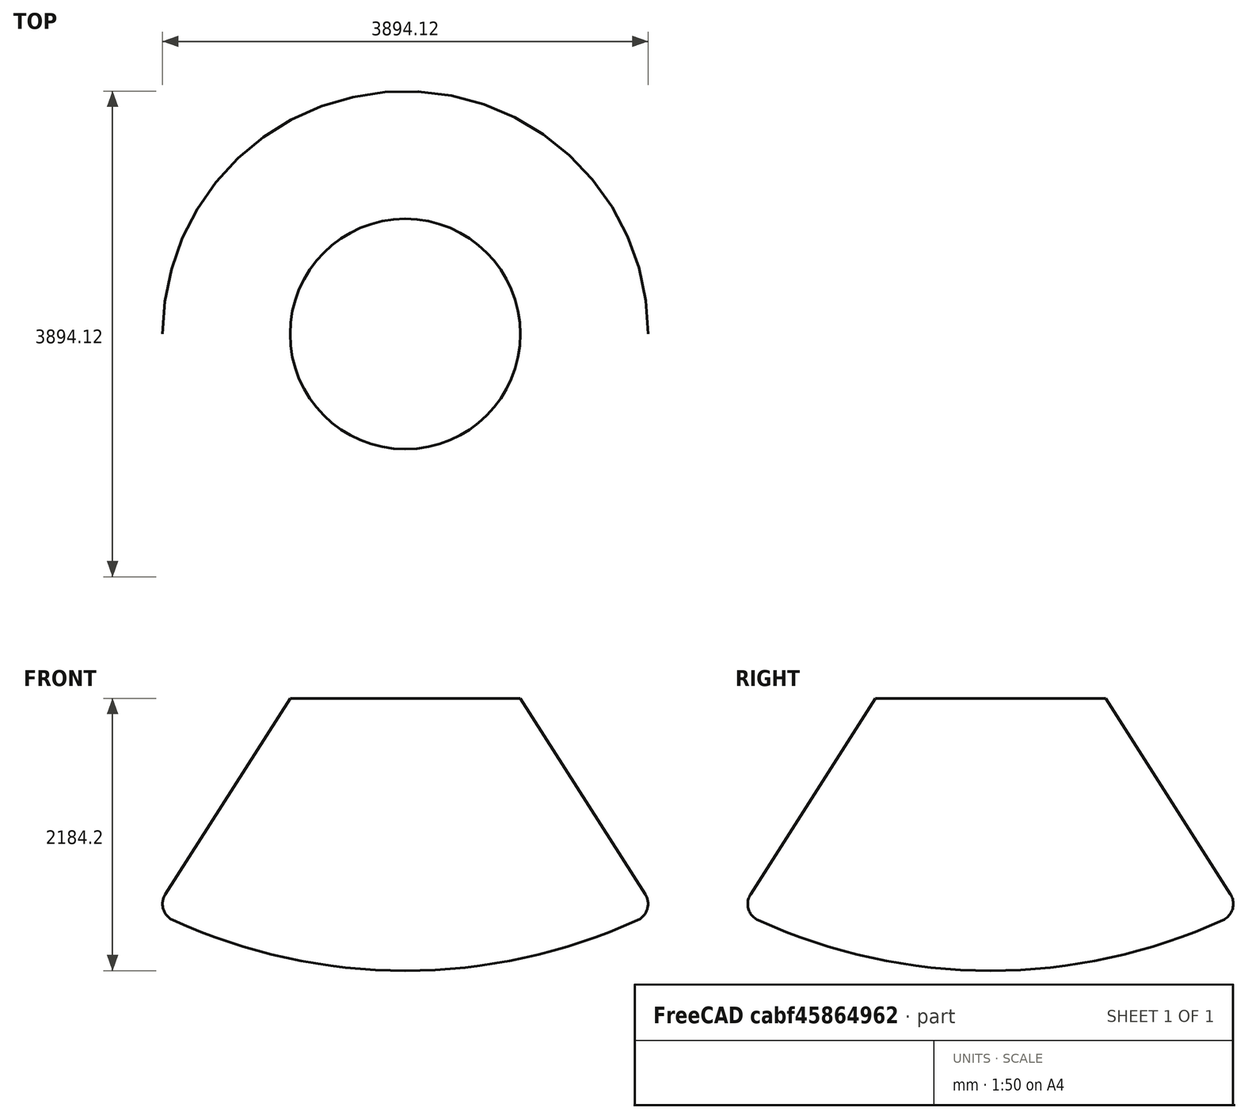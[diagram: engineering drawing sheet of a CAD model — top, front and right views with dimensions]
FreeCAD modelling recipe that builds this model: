
FCSTD DOCUMENT  (FreeCAD 0.21R33771 (Git))
Label: apollo
License: All rights reserved
LicenseURL: http://en.wikipedia.org/wiki/All_rights_reserved
objects: Part::Feature×2, Sketcher::SketchObject×1
note: 3 computed .brp shape members not serialized (recipe doc carries the construction recipe); baked Part::Feature solids carry a one-line shape summary decoded from their .brp

FEATURE [Sketcher::SketchObject] Sketch
  FullyConstrained = false
  MapMode = 5
  Placement = pos=(0,0,0) rot=(1,0,0;1.5708rad)
  sketch-geometry (11):
    g0: GeomPoint X=0 Y=3878 Z=0
    g1: Circle CenterX=0 CenterY=3878 CenterZ=0 NormalX=0 NormalY=0 NormalZ=1 AngleXU=0 Radius=4491
    g2: GeomPoint X=1924.5 Y=-1.42e-14 Z=0
    g3: LineSegment StartX=1924.5 StartY=-1.42e-14 StartZ=0 EndX=923.535 EndY=1571.2 EndZ=0
    g4: LineSegment StartX=923.535 StartY=1571.2 StartZ=0 EndX=0 EndY=1571.2 EndZ=0
    g5: ArcOfCircle CenterX=1803.01 CenterY=-77.3957 CenterZ=0 NormalX=0 NormalY=0 NormalZ=1 AngleXU=0 Radius=144.046 StartAngle=5.14009 EndAngle=6.85042
    g6: ArcOfCircle CenterX=0 CenterY=3878 CenterZ=0 NormalX=0 NormalY=0 NormalZ=1 AngleXU=0 Radius=4491 StartAngle=4.71239 EndAngle=5.14009
    g7: ArcOfCircle CenterX=0 CenterY=3878 CenterZ=0 NormalX=0 NormalY=0 NormalZ=1 AngleXU=0 Radius=4491 StartAngle=4.28469 EndAngle=4.71239
    g8: ArcOfCircle CenterX=-1803.01 CenterY=-77.3957 CenterZ=0 NormalX=0 NormalY=0 NormalZ=1 AngleXU=0 Radius=144.046 StartAngle=2.57436 EndAngle=4.28469
    g9: LineSegment StartX=-1924.5 StartY=-1.42e-14 StartZ=0 EndX=-923.535 EndY=1571.2 EndZ=0
    g10: LineSegment StartX=-923.535 StartY=1571.2 StartZ=0 EndX=0 EndY=1571.2 EndZ=0
  constraints (20):
    c: PointOnObject(g0,g-2)
    c: Coincident(g1,g0)
    c: PointOnObject(g2,g-1)
    c: Coincident(g3,g2)
    c: Angle(g3,g-1) = 1.00356
    c: DistanceY(g-1,g1) = 3878
    c: DistanceX(g-1,g3) = 1924.5
    c: DistanceY(g-1,g3) = 1571.2
    c: Diameter(g1) = 8982
    c: Coincident(g4,g3)
    c: PointOnObject(g4,g-2)
    c: Perpendicular(g-2,g4)
    c: Tangent(g5,g3) = -1.5708
    c: Tangent(g5,g1) = -1.5708
    c: Coincident(g6,g1)
    c: Coincident(g6,g5)
    c: Vertical(g6,g-1)
    c: Coincident(g10,g9)
    c: Tangent(g8,g9) = 1.5708
    c: Coincident(g7,g8)
FEATURE [Part::Feature] Wire001
  Placement = pos=(0,0,0) rot=(1,0,0;1.5708rad)
  shape: bbox 3894 x 2e-07 x 2184 mm, 0 faces, 0 solids (baked)
FEATURE [Part::Feature] Shell
  shape: bbox 4215 x 4215 x 2184 mm, 8 faces, 0 solids (baked)
